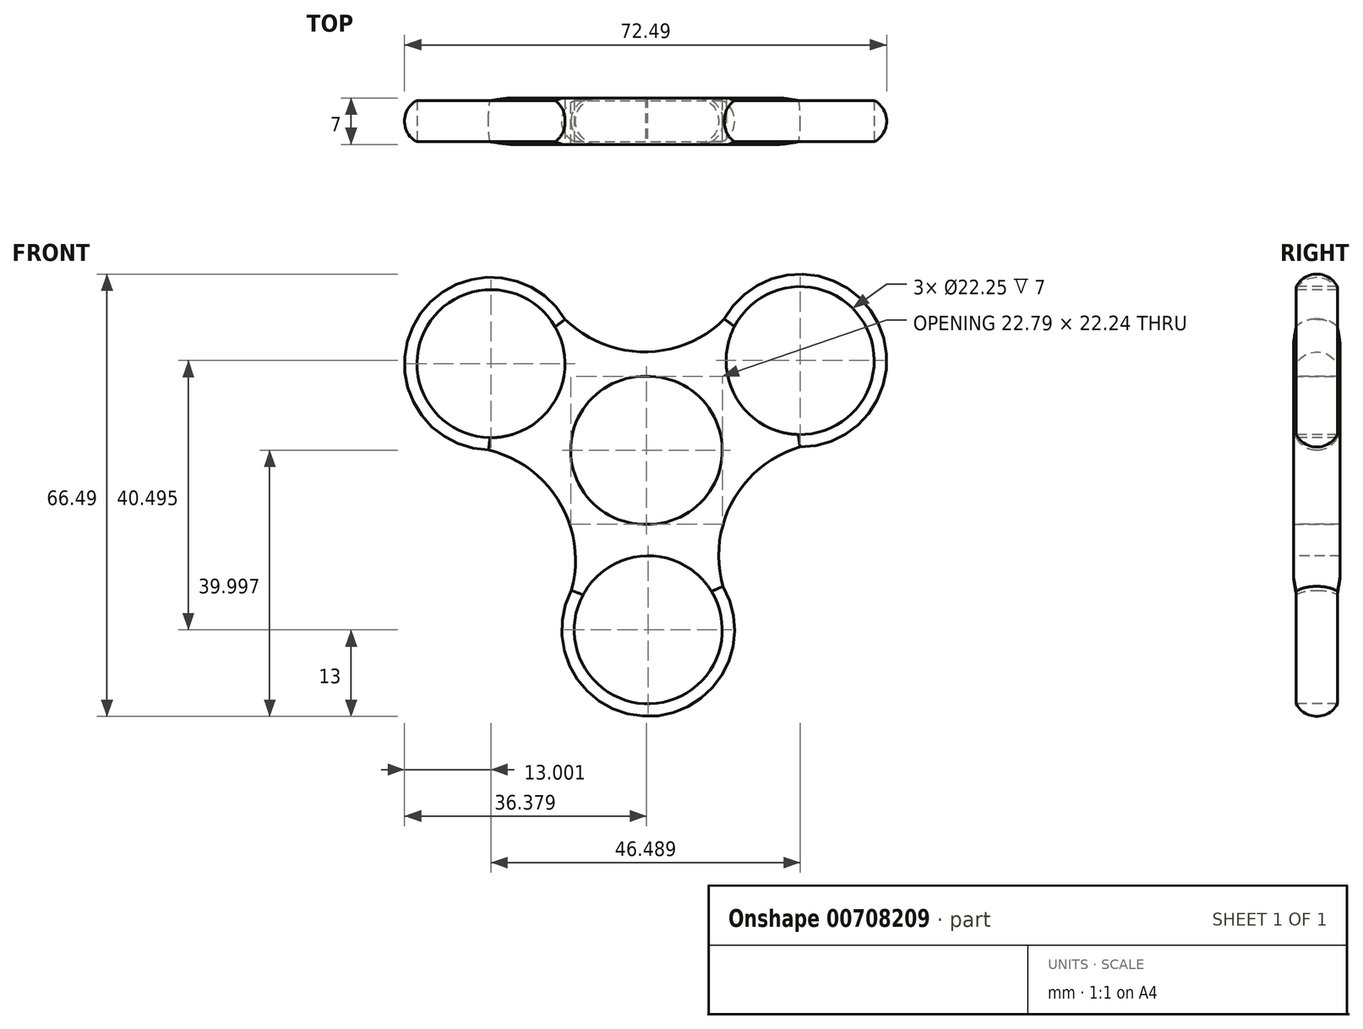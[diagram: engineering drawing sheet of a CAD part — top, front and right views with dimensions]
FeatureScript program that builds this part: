
annotation { "Feature Type Name" : "Feature", "Feature Type Description" : "" }
export const myFeature = defineFeature(function(context is Context, id is Id, definition is map)
    precondition{}
    {
        {
            var Q0;
            Q0=qCreatedBy(makeId("Front.planeOp"),FACE);
            var sketch = newSketch(context, id + "F0", { "sketchPlane" : qUnion([Q0])});
            skCircle(sketch, "E0", {"center": v(0, 0) * mm, "radius": 11.12 * mm});
            skCircle(sketch, "E1", {"center": v(0, -27) * mm, "radius": 13 * mm});
            skCircle(sketch, "E2.1.0", {"center": v(-0.54, 0) * mm, "radius": 11.12 * mm});
            skCircle(sketch, "E2.1.1", {"center": v(22.84, 13.5) * mm, "radius": 13 * mm});
            skCircle(sketch, "E2.2.0", {"center": v(-0.27, -0.47) * mm, "radius": 11.12 * mm});
            skCircle(sketch, "E2.2.1", {"center": v(-23.65, 13.03) * mm, "radius": 13 * mm});
            skPoint(sketch, "E2.center", {"position": v(-0.27, -0.16) * mm});
            skArc(sketch, "E3", {"start": v(-12.62, -23.87) * mm, "mid": v(-13.3, -7.86) * mm, "end": v(-27, 0.47) * mm});
            skArc(sketch, "E4", {"start": v(26.97, 1.17) * mm, "mid": v(12.84, -7.36) * mm, "end": v(12.62, -23.87) * mm});
            skArc(sketch, "E5", {"start": v(-14.82, 22.57) * mm, "mid": v(-0.25, 14.8) * mm, "end": v(14.04, 23.06) * mm});
            skSolve(sketch);
        }
        {
            var Q0;
            {var subQ0=sQuery(id+"F0.wireOp",EDGE,"E3");var subQ1=sQuery(id+"F0.wireOp",EDGE,"E2.2.1");var subQ2=makeQuery(id+"F0.imprint","INTERSECT",VERTEX,{"disambiguationData":[OD(1.0)],"derivedFrom":[subQ1,subQ0]});Q0=makeQuery(id+"F0.imprint","IMPRINT",FACE,{"disambiguationData":[TD([[makeQuery(id+"F0.imprint","IMPRINT",EDGE,{"disambiguationData":[TD([[subQ2,-1.0]])],"derivedFrom":subQ1}),1.0]])]});}
            var Q1;
            {var subQ0=sQuery(id+"F0.wireOp",EDGE,"E2.2.0");var subQ1=sQuery(id+"F0.wireOp",EDGE,"E0");var subQ2=makeQuery(id+"F0.imprint","INTERSECT",VERTEX,{"disambiguationData":[OD(0.0)],"derivedFrom":[subQ1,subQ0]});Q1=makeQuery(id+"F0.imprint","IMPRINT",FACE,{"disambiguationData":[TD([[makeQuery(id+"F0.imprint","IMPRINT",EDGE,{"disambiguationData":[TD([[subQ2,-1.0]])],"derivedFrom":subQ1}),1.0]])]});}
            var Q2;
            {var subQ0=sQuery(id+"F0.wireOp",EDGE,"E4");var subQ1=sQuery(id+"F0.wireOp",EDGE,"E2.1.1");var subQ2=makeQuery(id+"F0.imprint","INTERSECT",VERTEX,{"disambiguationData":[OD(0.0)],"derivedFrom":[subQ1,subQ0]});Q2=makeQuery(id+"F0.imprint","IMPRINT",FACE,{"disambiguationData":[TD([[makeQuery(id+"F0.imprint","IMPRINT",EDGE,{"disambiguationData":[TD([[subQ2,1.0]])],"derivedFrom":subQ1}),1.0]])]});}
            var Q3;
            {var subQ0=sQuery(id+"F0.wireOp",EDGE,"E5");var subQ1=sQuery(id+"F0.wireOp",EDGE,"E2.1.1");var subQ2=makeQuery(id+"F0.imprint","INTERSECT",VERTEX,{"disambiguationData":[OD(0.0)],"derivedFrom":[subQ1,subQ0]});Q3=makeQuery(id+"F0.imprint","IMPRINT",FACE,{"disambiguationData":[TD([[makeQuery(id+"F0.imprint","IMPRINT",EDGE,{"disambiguationData":[TD([[subQ2,-1.0]])],"derivedFrom":subQ1}),1.0]])]});}
            var Q4;
            {var subQ0=sQuery(id+"F0.wireOp",EDGE,"E4");var subQ1=sQuery(id+"F0.wireOp",EDGE,"E1");var subQ2=makeQuery(id+"F0.imprint","INTERSECT",VERTEX,{"disambiguationData":[OD(0.0)],"derivedFrom":[subQ1,subQ0]});Q4=makeQuery(id+"F0.imprint","IMPRINT",FACE,{"disambiguationData":[TD([[makeQuery(id+"F0.imprint","IMPRINT",EDGE,{"disambiguationData":[TD([[subQ2,-1.0]])],"derivedFrom":subQ1}),1.0]])]});}
            var Q5;
            {var subQ0=sQuery(id+"F0.wireOp",EDGE,"E2.1.0");var subQ1=sQuery(id+"F0.wireOp",EDGE,"E0");var subQ2=makeQuery(id+"F0.imprint","INTERSECT",VERTEX,{"disambiguationData":[OD(0.0)],"derivedFrom":[subQ1,subQ0]});Q5=makeQuery(id+"F0.imprint","IMPRINT",FACE,{"disambiguationData":[TD([[makeQuery(id+"F0.imprint","IMPRINT",EDGE,{"disambiguationData":[TD([[subQ2,1.0]])],"derivedFrom":subQ1}),-1.0]])]});}
            var Q6;
            {var subQ0=sQuery(id+"F0.wireOp",EDGE,"E2.1.0");var subQ1=sQuery(id+"F0.wireOp",EDGE,"E0");var subQ2=makeQuery(id+"F0.imprint","INTERSECT",VERTEX,{"disambiguationData":[OD(0.0)],"derivedFrom":[subQ1,subQ0]});Q6=makeQuery(id+"F0.imprint","IMPRINT",FACE,{"disambiguationData":[TD([[makeQuery(id+"F0.imprint","IMPRINT",EDGE,{"disambiguationData":[TD([[subQ2,1.0]])],"derivedFrom":subQ1}),1.0]])]});}
            var Q7;
            {var subQ0=sQuery(id+"F0.wireOp",EDGE,"E2.1.0");var subQ1=sQuery(id+"F0.wireOp",EDGE,"E0");var subQ2=makeQuery(id+"F0.imprint","INTERSECT",VERTEX,{"disambiguationData":[OD(1.0)],"derivedFrom":[subQ1,subQ0]});Q7=makeQuery(id+"F0.imprint","IMPRINT",FACE,{"disambiguationData":[TD([[makeQuery(id+"F0.imprint","IMPRINT",EDGE,{"disambiguationData":[TD([[subQ2,-1.0]])],"derivedFrom":subQ1}),1.0]])]});}
            var Q8;
            {var subQ0=sQuery(id+"F0.wireOp",EDGE,"E2.1.0");var subQ1=sQuery(id+"F0.wireOp",EDGE,"E0");var subQ2=makeQuery(id+"F0.imprint","INTERSECT",VERTEX,{"disambiguationData":[OD(1.0)],"derivedFrom":[subQ1,subQ0]});Q8=makeQuery(id+"F0.imprint","IMPRINT",FACE,{"disambiguationData":[TD([[makeQuery(id+"F0.imprint","IMPRINT",EDGE,{"disambiguationData":[TD([[subQ2,-1.0]])],"derivedFrom":subQ1}),-1.0]])]});}
            var Q9;
            {var subQ0=sQuery(id+"F0.wireOp",EDGE,"E2.2.0");var subQ1=sQuery(id+"F0.wireOp",EDGE,"E0");var subQ2=makeQuery(id+"F0.imprint","INTERSECT",VERTEX,{"disambiguationData":[OD(0.0)],"derivedFrom":[subQ1,subQ0]});Q9=makeQuery(id+"F0.imprint","IMPRINT",FACE,{"disambiguationData":[TD([[makeQuery(id+"F0.imprint","IMPRINT",EDGE,{"disambiguationData":[TD([[subQ2,-1.0]])],"derivedFrom":subQ1}),-1.0]])]});}
            var Q10;
            {var subQ0=sQuery(id+"F0.wireOp",EDGE,"E2.2.0");var subQ1=sQuery(id+"F0.wireOp",EDGE,"E0");var subQ2=makeQuery(id+"F0.imprint","INTERSECT",VERTEX,{"disambiguationData":[OD(0.0)],"derivedFrom":[subQ1,subQ0]});Q10=makeQuery(id+"F0.imprint","IMPRINT",FACE,{"disambiguationData":[TD([[makeQuery(id+"F0.imprint","IMPRINT",EDGE,{"disambiguationData":[TD([[subQ2,1.0]])],"derivedFrom":subQ1}),1.0]])]});}
            var Q11;
            {var subQ0=sQuery(id+"F0.wireOp",EDGE,"E2.2.0");var subQ1=sQuery(id+"F0.wireOp",EDGE,"E0");var subQ2=makeQuery(id+"F0.imprint","INTERSECT",VERTEX,{"disambiguationData":[OD(0.0)],"derivedFrom":[subQ1,subQ0]});Q11=makeQuery(id+"F0.imprint","IMPRINT",FACE,{"disambiguationData":[TD([[makeQuery(id+"F0.imprint","IMPRINT",EDGE,{"disambiguationData":[TD([[subQ2,1.0]])],"derivedFrom":subQ1}),-1.0]])]});}
            var Q12;
            {var subQ0=sQuery(id+"F0.wireOp",EDGE,"E5");var subQ1=sQuery(id+"F0.wireOp",EDGE,"E2.2.1");var subQ2=makeQuery(id+"F0.imprint","INTERSECT",VERTEX,{"disambiguationData":[OD(0.0)],"derivedFrom":[subQ1,subQ0]});Q12=makeQuery(id+"F0.imprint","IMPRINT",FACE,{"disambiguationData":[TD([[makeQuery(id+"F0.imprint","IMPRINT",EDGE,{"disambiguationData":[TD([[subQ2,1.0]])],"derivedFrom":subQ1}),1.0]])]});}
            var Q13;
            {var subQ0=sQuery(id+"F0.wireOp",EDGE,"E3");var subQ1=sQuery(id+"F0.wireOp",EDGE,"E2.2.1");var subQ2=makeQuery(id+"F0.imprint","INTERSECT",VERTEX,{"disambiguationData":[OD(0.0)],"derivedFrom":[subQ1,subQ0]});Q13=makeQuery(id+"F0.imprint","IMPRINT",FACE,{"disambiguationData":[TD([[makeQuery(id+"F0.imprint","IMPRINT",EDGE,{"disambiguationData":[TD([[subQ2,-1.0]])],"derivedFrom":subQ1}),1.0]])]});}
            var Q14;
            {var subQ0=sQuery(id+"F0.wireOp",EDGE,"E3");var subQ1=sQuery(id+"F0.wireOp",EDGE,"E1");var subQ2=makeQuery(id+"F0.imprint","INTERSECT",VERTEX,{"disambiguationData":[OD(0.0)],"derivedFrom":[subQ1,subQ0]});Q14=makeQuery(id+"F0.imprint","IMPRINT",FACE,{"disambiguationData":[TD([[makeQuery(id+"F0.imprint","IMPRINT",EDGE,{"disambiguationData":[TD([[subQ2,1.0]])],"derivedFrom":subQ1}),1.0]])]});}
            var Q15;
            {var subQ0=sQuery(id+"F0.wireOp",EDGE,"E5");var subQ1=sQuery(id+"F0.wireOp",EDGE,"E2.1.1");var subQ2=makeQuery(id+"F0.imprint","INTERSECT",VERTEX,{"disambiguationData":[OD(1.0)],"derivedFrom":[subQ1,subQ0]});Q15=makeQuery(id+"F0.imprint","IMPRINT",FACE,{"disambiguationData":[TD([[makeQuery(id+"F0.imprint","IMPRINT",EDGE,{"disambiguationData":[TD([[subQ2,-1.0]])],"derivedFrom":subQ1}),1.0]])]});}
            var Q16;
            {var subQ0=sQuery(id+"F0.wireOp",EDGE,"E4");var subQ1=sQuery(id+"F0.wireOp",EDGE,"E1");var subQ2=makeQuery(id+"F0.imprint","INTERSECT",VERTEX,{"disambiguationData":[OD(1.0)],"derivedFrom":[subQ1,subQ0]});Q16=makeQuery(id+"F0.imprint","IMPRINT",FACE,{"disambiguationData":[TD([[makeQuery(id+"F0.imprint","IMPRINT",EDGE,{"disambiguationData":[TD([[subQ2,-1.0]])],"derivedFrom":subQ1}),1.0]])]});}
            extrude(context, id + "F1", {"entities" : qUnion([Q0, Q1, Q2, Q3, Q4, Q5, Q6, Q7, Q8, Q9, Q10, Q11, Q12, Q13, Q14, Q15, Q16]), "depth" : 7 * mm, "offsetDistance" : 25 * mm});
        }
        {
            var Q0;
            Q0=makeQuery(id+"F1.opExtrude","CAP_FACE",FACE,{"disambiguationData":[OSD([sQuery(id+"F0.wireOp",EDGE,"E1"),sQuery(id+"F0.wireOp",EDGE,"E2.1.1"),sQuery(id+"F0.wireOp",EDGE,"E2.2.1"),sQuery(id+"F0.wireOp",EDGE,"E3"),sQuery(id+"F0.wireOp",EDGE,"E4"),sQuery(id+"F0.wireOp",EDGE,"E5")])],"isStart":false});
            var sketch = newSketch(context, id + "F2", { "sketchPlane" : qUnion([Q0])});
            skCircle(sketch, "E6", {"center": v(-23.65, 13.03) * mm, "radius": 11.12 * mm});
            skCircle(sketch, "E7", {"center": v(22.84, 13.5) * mm, "radius": 11.12 * mm});
            skCircle(sketch, "E8", {"center": v(0, -27) * mm, "radius": 11.12 * mm});
            skSolve(sketch);
        }
        {
            var Q0;
            Q0=makeQuery(id+"F2.imprint","IMPRINT",FACE,{"disambiguationData":[TD([[makeQuery(id+"F2.imprint","IMPRINT",EDGE,{"derivedFrom":sQuery(id+"F2.wireOp",EDGE,"E6")}),1.0]])]});
            var Q1;
            Q1=makeQuery(id+"F2.imprint","IMPRINT",FACE,{"disambiguationData":[TD([[makeQuery(id+"F2.imprint","IMPRINT",EDGE,{"derivedFrom":sQuery(id+"F2.wireOp",EDGE,"E7")}),1.0]])]});
            var Q2;
            Q2=makeQuery(id+"F2.imprint","IMPRINT",FACE,{"disambiguationData":[TD([[makeQuery(id+"F2.imprint","IMPRINT",EDGE,{"derivedFrom":sQuery(id+"F2.wireOp",EDGE,"E8")}),1.0]])]});
            extrude(context, id + "F3", {"entities" : qUnion([Q0, Q1, Q2]), "operationType" : NewBodyOperationType.REMOVE, "oppositeDirection" : true, "depth" : 25 * mm, "offsetDistance" : 25 * mm});
        }
        {
            var Q0;
            Q0=makeQuery(id+"F1.opExtrude","CAP_FACE",FACE,{"disambiguationData":[OSD([sQuery(id+"F0.wireOp",EDGE,"E1"),sQuery(id+"F0.wireOp",EDGE,"E2.1.1"),sQuery(id+"F0.wireOp",EDGE,"E2.2.1"),sQuery(id+"F0.wireOp",EDGE,"E3"),sQuery(id+"F0.wireOp",EDGE,"E4"),sQuery(id+"F0.wireOp",EDGE,"E5")])],"isStart":false});
            var sketch = newSketch(context, id + "F4", { "sketchPlane" : qUnion([Q0])});
            skCircle(sketch, "E9", {"center": v(0, 0) * mm, "radius": 11.12 * mm});
            skSolve(sketch);
        }
        {
            var Q0;
            Q0=makeQuery(id+"F4.imprint","IMPRINT",FACE,{"disambiguationData":[TD([[makeQuery(id+"F4.imprint","IMPRINT",EDGE,{"derivedFrom":sQuery(id+"F4.wireOp",EDGE,"E9")}),1.0]])]});
            extrude(context, id + "F5", {"entities" : qUnion([Q0]), "operationType" : NewBodyOperationType.REMOVE, "oppositeDirection" : true, "depth" : 25 * mm, "offsetDistance" : 25 * mm});
        }
        {
            var Q0;
            Q0=makeQuery(id+"F1.opExtrude","CAP_EDGE",EDGE,{"disambiguationData":[OSD([sQuery(id+"F0.wireOp",EDGE,"E2.2.1")])],"isStart":false});
            var Q1;
            Q1=makeQuery(id+"F1.opExtrude","CAP_EDGE",EDGE,{"disambiguationData":[OSD([sQuery(id+"F0.wireOp",EDGE,"E5")])],"isStart":false});
            var Q2;
            Q2=makeQuery(id+"F1.opExtrude","CAP_EDGE",EDGE,{"disambiguationData":[OSD([sQuery(id+"F0.wireOp",EDGE,"E2.1.1")])],"isStart":false});
            var Q3;
            Q3=makeQuery(id+"F1.opExtrude","CAP_EDGE",EDGE,{"disambiguationData":[OSD([sQuery(id+"F0.wireOp",EDGE,"E4")])],"isStart":false});
            var Q4;
            Q4=makeQuery(id+"F1.opExtrude","CAP_EDGE",EDGE,{"disambiguationData":[OSD([sQuery(id+"F0.wireOp",EDGE,"E3")])],"isStart":false});
            var Q5;
            Q5=makeQuery(id+"F1.opExtrude","CAP_EDGE",EDGE,{"disambiguationData":[OSD([sQuery(id+"F0.wireOp",EDGE,"E1")])],"isStart":false});
            var Q6;
            Q6=makeQuery(id+"F1.opExtrude","CAP_EDGE",EDGE,{"disambiguationData":[OSD([sQuery(id+"F0.wireOp",EDGE,"E5")])],"isStart":true});
            var Q7;
            Q7=makeQuery(id+"F1.opExtrude","CAP_EDGE",EDGE,{"disambiguationData":[OSD([sQuery(id+"F0.wireOp",EDGE,"E2.1.1")])],"isStart":true});
            var Q8;
            Q8=makeQuery(id+"F1.opExtrude","CAP_EDGE",EDGE,{"disambiguationData":[OSD([sQuery(id+"F0.wireOp",EDGE,"E2.2.1")])],"isStart":true});
            var Q9;
            Q9=makeQuery(id+"F1.opExtrude","CAP_EDGE",EDGE,{"disambiguationData":[OSD([sQuery(id+"F0.wireOp",EDGE,"E3")])],"isStart":true});
            var Q10;
            Q10=makeQuery(id+"F1.opExtrude","CAP_EDGE",EDGE,{"disambiguationData":[OSD([sQuery(id+"F0.wireOp",EDGE,"E4")])],"isStart":true});
            var Q11;
            Q11=makeQuery(id+"F1.opExtrude","CAP_EDGE",EDGE,{"disambiguationData":[OSD([sQuery(id+"F0.wireOp",EDGE,"E1")])],"isStart":true});
            fillet(context, id + "F6", {"entities" : qUnion([Q0, Q1, Q2, Q3, Q4, Q5, Q6, Q7, Q8, Q9, Q10, Q11]), "radius" : 3.5 * mm, "tangentPropagation" : true, "allowEdgeOverflow" : false});
        }
    });
